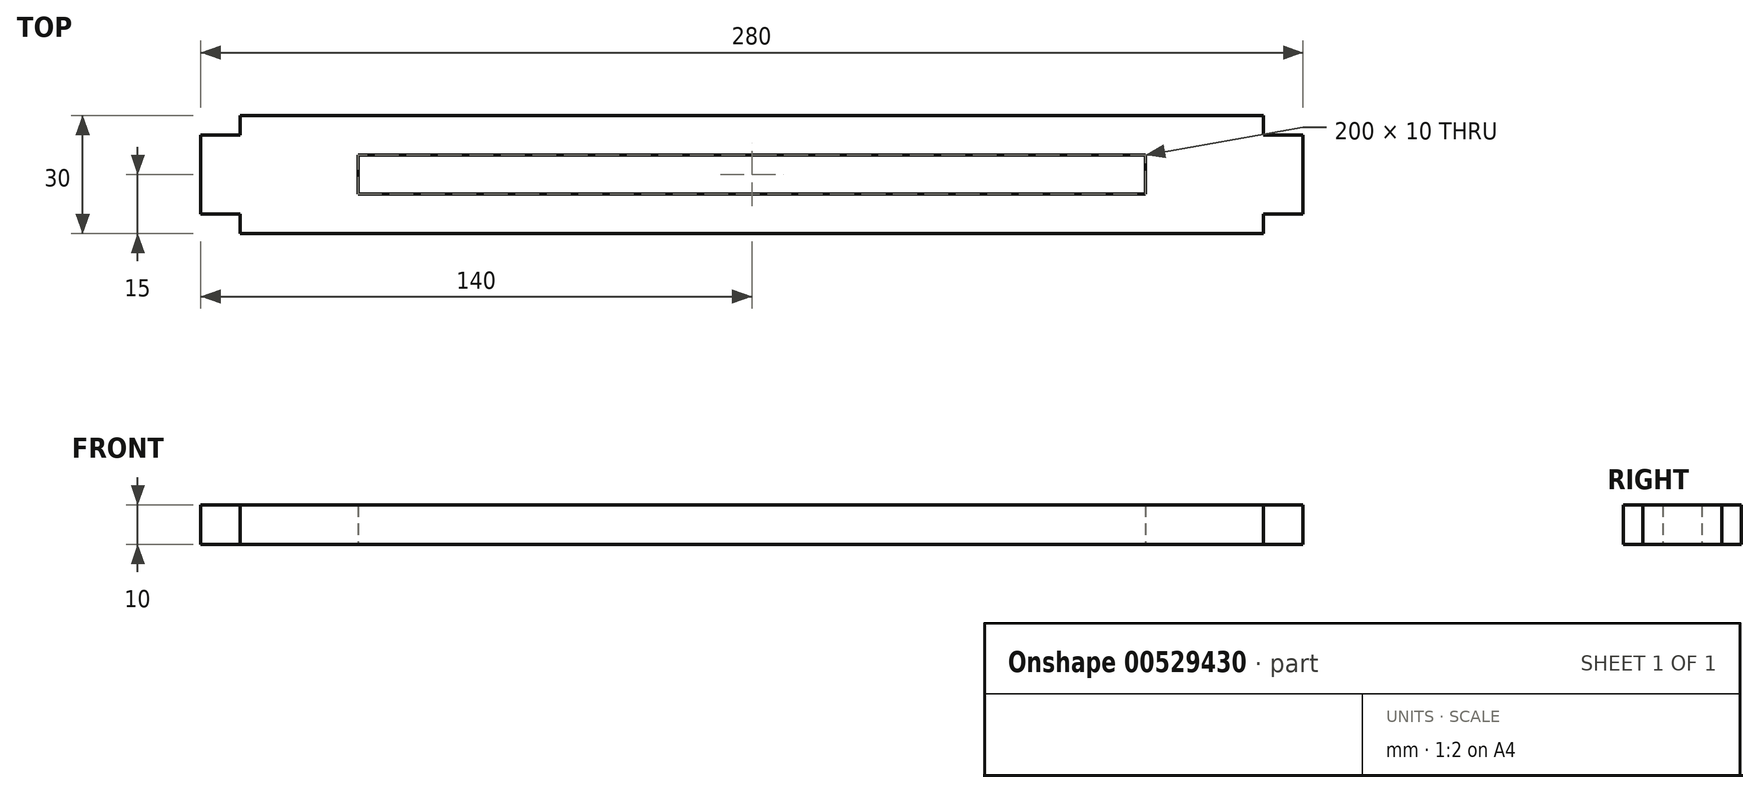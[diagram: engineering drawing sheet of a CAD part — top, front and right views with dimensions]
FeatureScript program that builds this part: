
annotation { "Feature Type Name" : "Feature", "Feature Type Description" : "" }
export const myFeature = defineFeature(function(context is Context, id is Id, definition is map)
    precondition{}
    {
        {
            var Q0;
            Q0=qCreatedBy(makeId("Top.planeOp"),FACE);
            var sketch = newSketch(context, id + "F0", { "sketchPlane" : qUnion([Q0])});
            skLineSegment(sketch, "E0.bottom", {"start": v(130, -15) * mm, "end": v(-130, -15) * mm});
            skLineSegment(sketch, "E0.top", {"start": v(130, 15) * mm, "end": v(-130, 15) * mm});
            skPoint(sketch, "E0.middle", {"position": v(0, 0) * mm});
            skLineSegment(sketch, "E1", {"start": v(-130, 15) * mm, "end": v(-130, 10) * mm});
            skLineSegment(sketch, "E2", {"start": v(-130, 10) * mm, "end": v(-140, 10) * mm});
            skLineSegment(sketch, "E3", {"start": v(-140, 10) * mm, "end": v(-140, -10) * mm});
            skLineSegment(sketch, "E4", {"start": v(-140, -10) * mm, "end": v(-130, -10) * mm});
            skLineSegment(sketch, "E5", {"start": v(-130, -10) * mm, "end": v(-130, -15) * mm});
            skLineSegment(sketch, "E6.MirrorCS", {"start": v(130, 15) * mm, "end": v(130, 10) * mm});
            skLineSegment(sketch, "E7.MirrorCS", {"start": v(140, 10) * mm, "end": v(140, -10) * mm});
            skLineSegment(sketch, "E8.MirrorCS", {"start": v(130, -10) * mm, "end": v(130, -15) * mm});
            skLineSegment(sketch, "E9.MirrorCS", {"start": v(140, -10) * mm, "end": v(130, -10) * mm});
            skLineSegment(sketch, "E10.MirrorCS", {"start": v(130, 10) * mm, "end": v(140, 10) * mm});
            skLineSegment(sketch, "E11.bottom", {"start": v(100, -5) * mm, "end": v(-100, -5) * mm});
            skLineSegment(sketch, "E11.top", {"start": v(100, 5) * mm, "end": v(-100, 5) * mm});
            skLineSegment(sketch, "E11.left", {"start": v(100, -5) * mm, "end": v(100, 5) * mm});
            skLineSegment(sketch, "E11.right", {"start": v(-100, -5) * mm, "end": v(-100, 5) * mm});
            skSolve(sketch);
        }
        {
            var Q0;
            Q0=makeQuery(id+"F0.imprint","IMPRINT",FACE,{"disambiguationData":[TD([[makeQuery(id+"F0.imprint","IMPRINT",EDGE,{"derivedFrom":sQuery(id+"F0.wireOp",EDGE,"E0.bottom")}),-1.0]])]});
            extrude(context, id + "F1", {"entities" : qUnion([Q0]), "depth" : 10 * mm, "offsetDistance" : 25 * mm});
        }
    });
